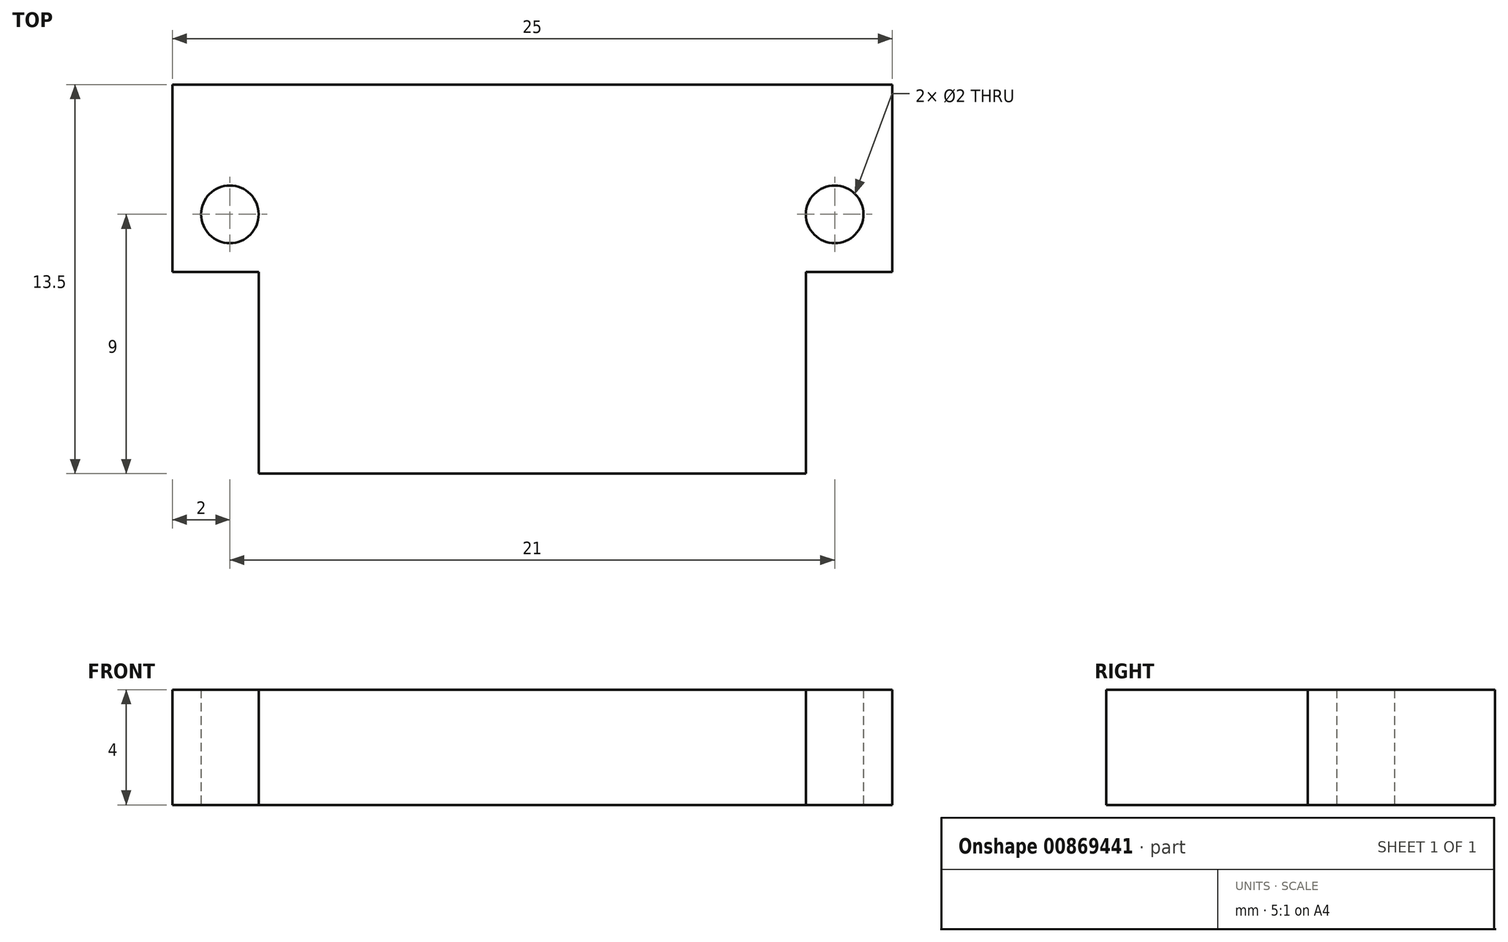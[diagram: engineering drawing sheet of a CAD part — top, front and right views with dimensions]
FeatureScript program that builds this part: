
annotation { "Feature Type Name" : "Feature", "Feature Type Description" : "" }
export const myFeature = defineFeature(function(context is Context, id is Id, definition is map)
    precondition{}
    {
        {
            var Q0;
            Q0=qCreatedBy(makeId("Top.planeOp"),FACE);
            var sketch = newSketch(context, id + "F0", { "sketchPlane" : qUnion([Q0])});
            skLineSegment(sketch, "E0", {"start": v(0, 13.5) * mm, "end": v(-12.5, 13.5) * mm});
            skLineSegment(sketch, "E1", {"start": v(-12.5, 13.5) * mm, "end": v(-12.5, 7) * mm});
            skLineSegment(sketch, "E2", {"start": v(-12.5, 7) * mm, "end": v(-9.5, 7) * mm});
            skLineSegment(sketch, "E3", {"start": v(-9.5, 7) * mm, "end": v(-9.5, 0) * mm});
            skLineSegment(sketch, "E4", {"start": v(-9.5, 0) * mm, "end": v(0, 0) * mm});
            skCircle(sketch, "E5", {"center": v(-10.5, 9) * mm, "radius": 1 * mm});
            skLineSegment(sketch, "E6.MirrorCS", {"start": v(0, 13.5) * mm, "end": v(12.5, 13.5) * mm});
            skLineSegment(sketch, "E7.MirrorCS", {"start": v(12.5, 13.5) * mm, "end": v(12.5, 7) * mm});
            skLineSegment(sketch, "E8.MirrorCS", {"start": v(12.5, 7) * mm, "end": v(9.5, 7) * mm});
            skLineSegment(sketch, "E9.MirrorCS", {"start": v(9.5, 7) * mm, "end": v(9.5, 0) * mm});
            skLineSegment(sketch, "E10.MirrorCS", {"start": v(9.5, 0) * mm, "end": v(0, 0) * mm});
            skCircle(sketch, "E11.MirrorC", {"center": v(10.5, 9) * mm, "radius": 1 * mm});
            skSolve(sketch);
        }
        {
            var Q0;
            Q0=makeQuery(id+"F0.imprint","IMPRINT",FACE,{"disambiguationData":[TD([[makeQuery(id+"F0.imprint","IMPRINT",EDGE,{"derivedFrom":sQuery(id+"F0.wireOp",EDGE,"E0")}),1.0]])]});
            extrude(context, id + "F1", {"entities" : qUnion([Q0]), "depth" : 4 * mm, "offsetDistance" : 25 * mm});
        }
    });
